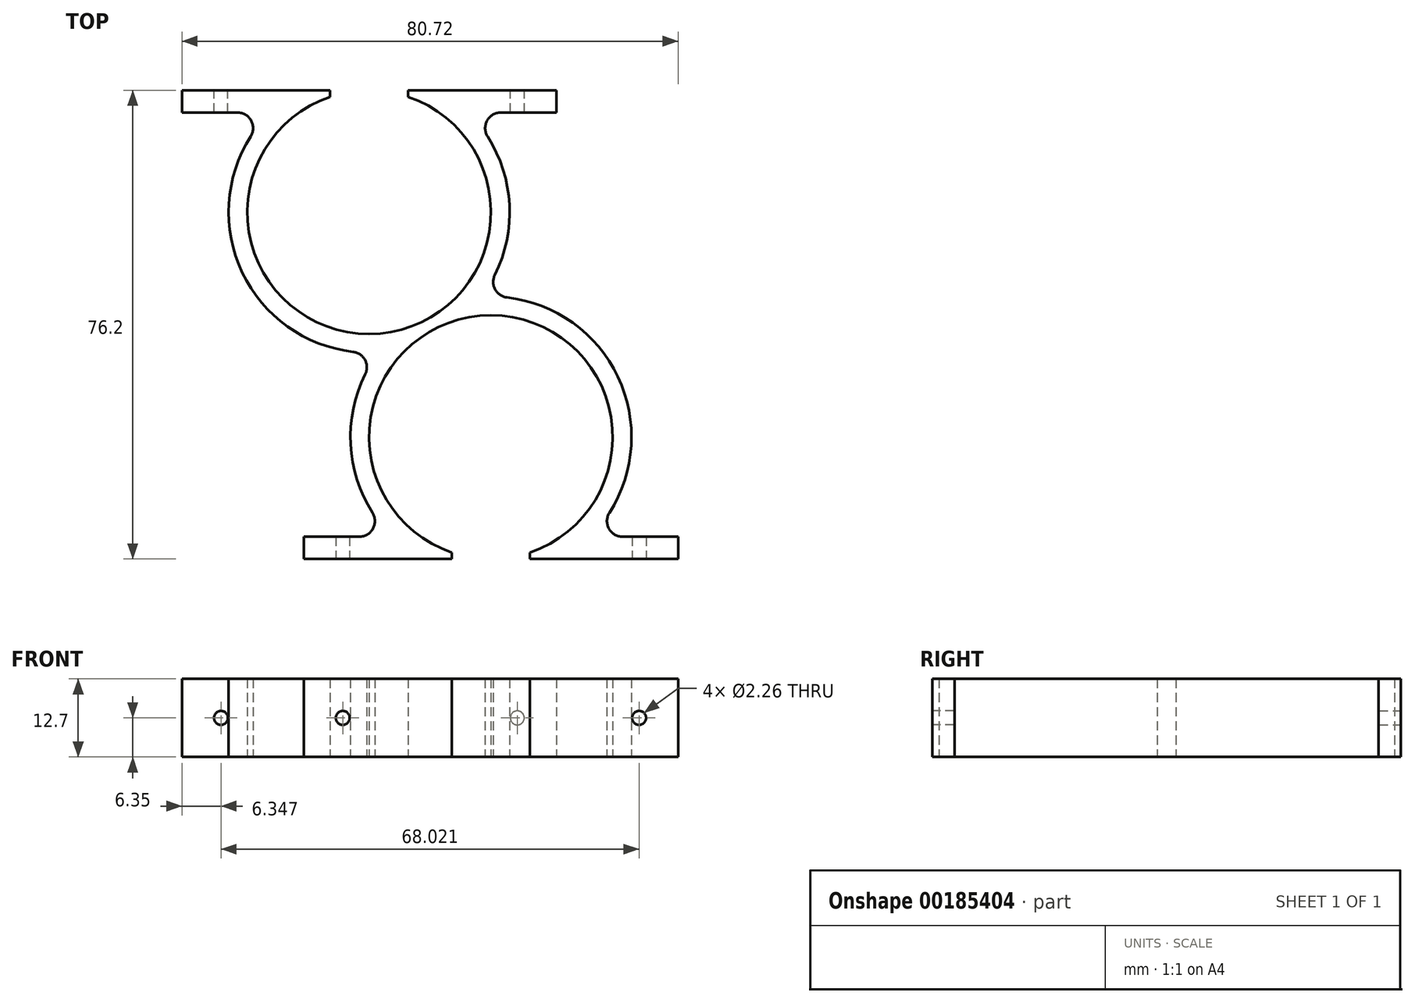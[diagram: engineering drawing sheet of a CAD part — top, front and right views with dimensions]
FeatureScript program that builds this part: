
annotation { "Feature Type Name" : "Feature", "Feature Type Description" : "" }
export const myFeature = defineFeature(function(context is Context, id is Id, definition is map)
    precondition{}
    {
        {
            var Q0;
            Q0=qCreatedBy(makeId("Top.planeOp"),FACE);
            var sketch = newSketch(context, id + "F0", { "sketchPlane" : qUnion([Q0])});
            skLineSegment(sketch, "E0.bottom", {"start": v(50.8, -38.1) * mm, "end": v(19.28, -38.1) * mm});
            skLineSegment(sketch, "E0.top", {"start": v(50.8, 38.1) * mm, "end": v(-0.53, 38.1) * mm});
            skLineSegment(sketch, "E0.left", {"start": v(50.8, -38.1) * mm, "end": v(50.8, 38.1) * mm});
            skLineSegment(sketch, "E0.right", {"start": v(-50.8, -38.1) * mm, "end": v(-50.8, 6.88) * mm});
            skPoint(sketch, "E0.middle", {"position": v(0, 0) * mm});
            skPoint(sketch, "E1.end.orphan", {"position": v(-30.99, 0) * mm});
            skLineSegment(sketch, "E2", {"start": v(-30.99, 38.1) * mm, "end": v(-30.99, 18.29) * mm});
            skArc(sketch, "E3", {"start": v(-37.34, 37.05) * mm, "mid": v(-30.99, -1.52) * mm, "end": v(-24.64, 37.05) * mm});
            skLineSegment(sketch, "E4", {"start": v(-50.8, -38.1) * mm, "end": v(-41.63, -38.1) * mm});
            skLineSegment(sketch, "E5", {"start": v(-11.18, -38.1) * mm, "end": v(-11.18, -18.29) * mm});
            skArc(sketch, "E6", {"start": v(-4.83, -37.05) * mm, "mid": v(-11.18, 1.52) * mm, "end": v(-17.53, -37.05) * mm});
            skArc(sketch, "E7.0", {"start": v(-10.53, 8.08) * mm, "mid": v(-8.16, 19.49) * mm, "end": v(-11.72, 30.58) * mm});
            skArc(sketch, "E8.0", {"start": v(-31.63, -8.08) * mm, "mid": v(-34, -19.49) * mm, "end": v(-30.45, -30.58) * mm});
            skArc(sketch, "E9.trimOffspring", {"start": v(8.1, -30.58) * mm, "mid": v(9.47, -8.47) * mm, "end": v(-8.55, 4.42) * mm});
            skArc(sketch, "E10.trimOffspring", {"start": v(-50.26, 30.58) * mm, "mid": v(-51.63, 8.47) * mm, "end": v(-33.61, -4.42) * mm});
            skPoint(sketch, "E11.visualSharp", {"position": v(-12.74, 4.52) * mm});
            skArc(sketch, "E11.filletArc", {"start": v(-10.53, 8.08) * mm, "mid": v(-10.5, 5.73) * mm, "end": v(-8.55, 4.42) * mm});
            skPoint(sketch, "E12.visualSharp", {"position": v(-29.42, -4.52) * mm});
            skArc(sketch, "E12.filletArc", {"start": v(-31.63, -8.08) * mm, "mid": v(-31.67, -5.73) * mm, "end": v(-33.61, -4.42) * mm});
            skLineSegment(sketch, "E13", {"start": v(-22.58, -38.1) * mm, "end": v(-22.58, -40.64) * mm});
            skLineSegment(sketch, "E14", {"start": v(-22.58, -40.64) * mm, "end": v(-40.26, -40.64) * mm});
            skLineSegment(sketch, "E15", {"start": v(-32.59, -34.49) * mm, "end": v(-41.63, -34.49) * mm});
            skLineSegment(sketch, "E16", {"start": v(-41.63, -34.49) * mm, "end": v(-41.63, -38.1) * mm});
            skLineSegment(sketch, "E17.MirrorCS", {"start": v(4.95, -34.49) * mm, "end": v(19.28, -34.49) * mm});
            skLineSegment(sketch, "E18.MirrorCS", {"start": v(10.24, -34.49) * mm, "end": v(19.28, -34.49) * mm});
            skLineSegment(sketch, "E19.MirrorCS", {"start": v(19.28, -34.49) * mm, "end": v(19.28, -38.1) * mm});
            skLineSegment(sketch, "E20.MirrorCS", {"start": v(28.45, -38.1) * mm, "end": v(19.28, -38.1) * mm});
            skPoint(sketch, "E21.orphan", {"position": v(-22.58, -34.49) * mm});
            skPoint(sketch, "E22.orphan", {"position": v(0.23, -34.49) * mm});
            skPoint(sketch, "E23.MirrorCS.start.orphan", {"position": v(0.23, -38.1) * mm});
            skPoint(sketch, "E24.visualSharp", {"position": v(-27.3, -34.49) * mm});
            skArc(sketch, "E24.filletArc", {"start": v(-32.59, -34.49) * mm, "mid": v(-30.36, -33.17) * mm, "end": v(-30.45, -30.58) * mm});
            skPoint(sketch, "E25.visualSharp", {"position": v(4.95, -34.49) * mm});
            skArc(sketch, "E25.filletArc", {"start": v(8.1, -30.58) * mm, "mid": v(8.01, -33.17) * mm, "end": v(10.24, -34.49) * mm});
            skLineSegment(sketch, "E26", {"start": v(-52.4, 34.49) * mm, "end": v(-61.44, 34.49) * mm});
            skLineSegment(sketch, "E27", {"start": v(-61.44, 38.1) * mm, "end": v(-61.44, 34.49) * mm});
            skLineSegment(sketch, "E28", {"start": v(-9.57, 34.49) * mm, "end": v(-0.53, 34.49) * mm});
            skLineSegment(sketch, "E29", {"start": v(-0.53, 34.49) * mm, "end": v(-0.53, 38.1) * mm});
            skPoint(sketch, "E29.endSnap0", {"position": v(0, 38.1) * mm});
            skPoint(sketch, "E30.visualSharp", {"position": v(-47.12, 34.49) * mm});
            skArc(sketch, "E30.filletArc", {"start": v(-50.26, 30.58) * mm, "mid": v(-50.17, 33.17) * mm, "end": v(-52.4, 34.49) * mm});
            skPoint(sketch, "E31.visualSharp", {"position": v(-14.86, 34.49) * mm});
            skArc(sketch, "E31.filletArc", {"start": v(-9.57, 34.49) * mm, "mid": v(-11.8, 33.17) * mm, "end": v(-11.72, 30.58) * mm});
            skLineSegment(sketch, "E32", {"start": v(-30.99, 18.29) * mm, "end": v(-37.34, 18.29) * mm});
            skLineSegment(sketch, "E33", {"start": v(-37.34, 18.29) * mm, "end": v(-37.34, 38.1) * mm});
            skLineSegment(sketch, "E34.MirrorCS", {"start": v(-24.64, 18.29) * mm, "end": v(-24.64, 38.1) * mm});
            skPoint(sketch, "E35.start.orphan", {"position": v(-50.8, 38.1) * mm});
            skLineSegment(sketch, "E36", {"start": v(-11.18, -18.29) * mm, "end": v(-4.83, -18.29) * mm});
            skLineSegment(sketch, "E37", {"start": v(-4.83, -18.29) * mm, "end": v(-4.83, -38.1) * mm});
            skLineSegment(sketch, "E38.MirrorCS", {"start": v(-17.53, -18.29) * mm, "end": v(-17.53, -38.1) * mm});
            skPoint(sketch, "E39.orphan", {"position": v(-11.18, -38.1) * mm});
            skLineSegment(sketch, "E40.trimOffspring", {"start": v(0.23, -38.1) * mm, "end": v(-4.83, -38.1) * mm});
            skLineSegment(sketch, "E41.trimOffspring", {"start": v(-41.63, -38.1) * mm, "end": v(-50.8, -38.1) * mm});
            skLineSegment(sketch, "E42", {"start": v(-41.63, -38.1) * mm, "end": v(-17.53, -38.1) * mm});
            skLineSegment(sketch, "E43", {"start": v(-4.83, -38.1) * mm, "end": v(19.28, -38.1) * mm});
            skLineSegment(sketch, "E44", {"start": v(-0.53, 38.1) * mm, "end": v(-24.64, 38.1) * mm});
            skLineSegment(sketch, "E45", {"start": v(-61.44, 38.1) * mm, "end": v(-37.34, 38.1) * mm});
            skSolve(sketch);
        }
        {
            var Q0;
            {var subQ1=sQuery(id+"F0.wireOp",EDGE,"E3");Q0=makeQuery(id+"F0.imprint","IMPRINT",FACE,{"disambiguationData":[TD([[makeQuery(id+"F0.imprint","IMPRINT",EDGE,{"derivedFrom":subQ1}),-1.0]])]});}
            extrude(context, id + "F1", {"entities" : qUnion([Q0]), "depth" : 12.7 * mm});
        }
        {
            var Q0;
            Q0=makeQuery(id+"F1.opExtrude","SWEPT_FACE",FACE,{"disambiguationData":[OSD([sQuery(id+"F0.wireOp",EDGE,"E42")])]});
            var sketch = newSketch(context, id + "F2", { "sketchPlane" : qUnion([Q0])});
            skLineSegment(sketch, "E46", {"start": v(-41.63, 12.7) * mm, "end": v(-41.63, 6.35) * mm});
            skLineSegment(sketch, "E47", {"start": v(-41.63, 6.35) * mm, "end": v(-35.28, 6.35) * mm});
            skSolve(sketch);
        }
        {
            var Q0;
            Q0=makeQuery(id+"F1.opExtrude","SWEPT_FACE",FACE,{"disambiguationData":[OSD([sQuery(id+"F0.wireOp",EDGE,"E43")])]});
            var sketch = newSketch(context, id + "F3", { "sketchPlane" : qUnion([Q0])});
            skLineSegment(sketch, "E48", {"start": v(19.28, 12.7) * mm, "end": v(19.28, 6.35) * mm});
            skLineSegment(sketch, "E49", {"start": v(19.28, 6.35) * mm, "end": v(12.93, 6.35) * mm});
            skSolve(sketch);
        }
        {
            var Q0;
            Q0=makeQuery(id+"F1.opExtrude","SWEPT_FACE",FACE,{"disambiguationData":[OSD([sQuery(id+"F0.wireOp",EDGE,"E45")])]});
            var sketch = newSketch(context, id + "F4", { "sketchPlane" : qUnion([Q0])});
            skLineSegment(sketch, "E50", {"start": v(61.44, 0) * mm, "end": v(61.44, 6.35) * mm});
            skLineSegment(sketch, "E51", {"start": v(61.44, 6.35) * mm, "end": v(55.1, 6.35) * mm});
            skSolve(sketch);
        }
        {
            var Q0;
            Q0=makeQuery(id+"F1.opExtrude","SWEPT_FACE",FACE,{"disambiguationData":[OSD([sQuery(id+"F0.wireOp",EDGE,"E44")])]});
            var sketch = newSketch(context, id + "F5", { "sketchPlane" : qUnion([Q0])});
            skLineSegment(sketch, "E52", {"start": v(0.53, 0) * mm, "end": v(0.53, 6.35) * mm});
            skLineSegment(sketch, "E53", {"start": v(0.53, 6.35) * mm, "end": v(6.88, 6.35) * mm});
            skSolve(sketch);
        }
        {
            var Q0;
            Q0=sQuery(id+"F4.wireOp",VERTEX,"E51.end");
            var Q1;
            Q1=sQuery(id+"F5.wireOp",VERTEX,"E53.end");
            var Q2;
            Q2=sQuery(id+"F2.wireOp",VERTEX,"E47.end");
            var Q3;
            Q3=sQuery(id+"F3.wireOp",VERTEX,"E49.end");
            var Q4;
            Q4=makeQuery(id+"F1.opExtrude","SWEPT_BODY",BODY,{"disambiguationData":[OSD([sQuery(id+"F0.wireOp",EDGE,"E3"),sQuery(id+"F0.wireOp",EDGE,"E6"),sQuery(id+"F0.wireOp",EDGE,"E7.0"),sQuery(id+"F0.wireOp",EDGE,"E8.0"),sQuery(id+"F0.wireOp",EDGE,"E9.trimOffspring"),sQuery(id+"F0.wireOp",EDGE,"E10.trimOffspring"),sQuery(id+"F0.wireOp",EDGE,"E11.filletArc"),sQuery(id+"F0.wireOp",EDGE,"E12.filletArc"),sQuery(id+"F0.wireOp",EDGE,"E15"),sQuery(id+"F0.wireOp",EDGE,"E16"),sQuery(id+"F0.wireOp",EDGE,"E18.MirrorCS"),sQuery(id+"F0.wireOp",EDGE,"E19.MirrorCS"),sQuery(id+"F0.wireOp",EDGE,"E24.filletArc"),sQuery(id+"F0.wireOp",EDGE,"E25.filletArc"),sQuery(id+"F0.wireOp",EDGE,"E26"),sQuery(id+"F0.wireOp",EDGE,"E27"),sQuery(id+"F0.wireOp",EDGE,"E28"),sQuery(id+"F0.wireOp",EDGE,"E29"),sQuery(id+"F0.wireOp",EDGE,"E30.filletArc"),sQuery(id+"F0.wireOp",EDGE,"E31.filletArc"),sQuery(id+"F0.wireOp",EDGE,"E33"),sQuery(id+"F0.wireOp",EDGE,"E34.MirrorCS"),sQuery(id+"F0.wireOp",EDGE,"E37"),sQuery(id+"F0.wireOp",EDGE,"E38.MirrorCS"),sQuery(id+"F0.wireOp",EDGE,"E42"),sQuery(id+"F0.wireOp",EDGE,"E43"),sQuery(id+"F0.wireOp",EDGE,"E44"),sQuery(id+"F0.wireOp",EDGE,"E45")])]});
            hole(context, id + "F6", {"style" : HoleStyle.SIMPLE, "endStyle" : HoleEndStyle.BLIND, "standardTappedOrClearance" : lookupTablePath({ "standard" : "ANSI", "fit" : "Close", "engagement" : "75%", "pitch" : "40 tpi", "size" : "#4", "type" : "Tapped" }), "standardBlindInLast" : lookupTablePath({ "fit" : "Close", "standard" : "ANSI", "engagement" : "75%", "pitch" : "40 tpi", "size" : "#4", "type" : "Tapped" }), "holeDiameter" : 2.26 * mm, "holeDepth" : 12.7 * mm, "locations" : qUnion([Q0, Q1, Q2, Q3]), "scope" : qUnion([Q4]), "majorDiameter" : 2.84 * mm});
        }
    });
